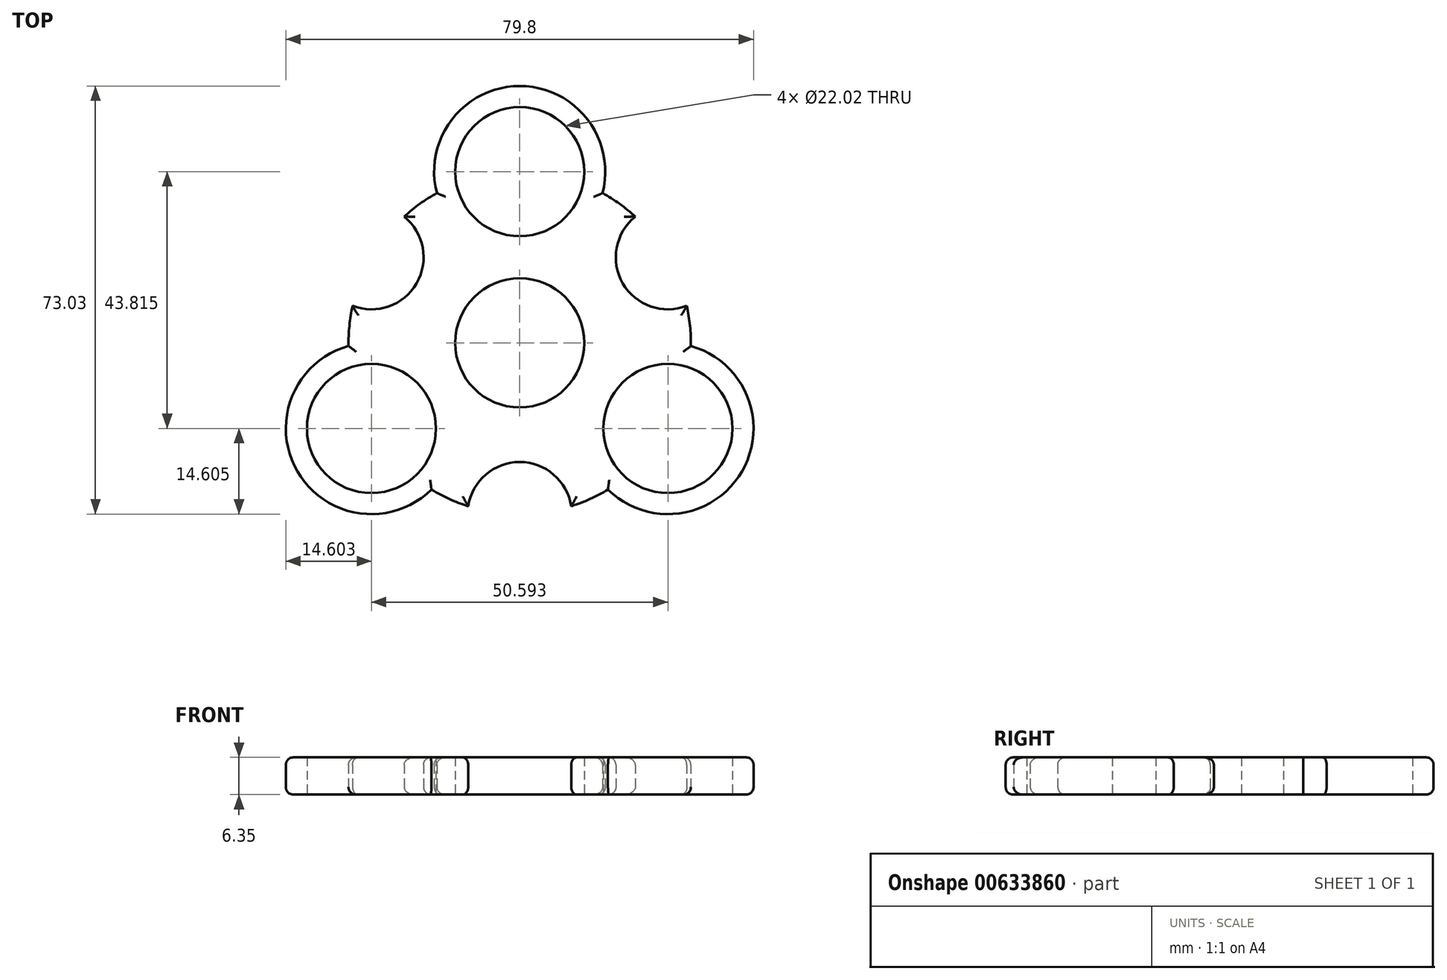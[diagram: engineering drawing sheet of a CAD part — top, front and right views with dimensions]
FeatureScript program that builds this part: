
annotation { "Feature Type Name" : "Feature", "Feature Type Description" : "" }
export const myFeature = defineFeature(function(context is Context, id is Id, definition is map)
    precondition{}
    {
        {
            var Q0;
            Q0=qCreatedBy(makeId("Top.planeOp"),FACE);
            var sketch = newSketch(context, id + "F0", { "sketchPlane" : qUnion([Q0])});
            skCircle(sketch, "E0", {"center": v(0, 0) * mm, "radius": 11.01 * mm});
            skCircle(sketch, "E1", {"center": v(0, 0) * mm, "radius": 14.6 * mm});
            skLineSegment(sketch, "E2", {"start": v(0, 0) * mm, "end": v(0, 29.21) * mm});
            skLineSegment(sketch, "E3", {"start": v(0, 0) * mm, "end": v(-25.3, -14.6) * mm});
            skLineSegment(sketch, "E4", {"start": v(0, 0) * mm, "end": v(25.3, -14.6) * mm});
            skCircle(sketch, "E5", {"center": v(0, 29.21) * mm, "radius": 11.01 * mm});
            skCircle(sketch, "E6", {"center": v(0, 29.21) * mm, "radius": 14.6 * mm});
            skCircle(sketch, "E7", {"center": v(-25.3, -14.6) * mm, "radius": 11.01 * mm});
            skCircle(sketch, "E8", {"center": v(25.3, -14.6) * mm, "radius": 11.01 * mm});
            skCircle(sketch, "E9", {"center": v(25.3, -14.6) * mm, "radius": 14.6 * mm});
            skCircle(sketch, "E10", {"center": v(-25.3, -14.6) * mm, "radius": 14.6 * mm});
            skArc(sketch, "E11", {"start": v(-14.14, 25.56) * mm, "mid": v(-25.3, 14.6) * mm, "end": v(-29.2, -0.53) * mm});
            skArc(sketch, "E12.trimOffspring", {"start": v(29.2, -0.53) * mm, "mid": v(25.3, 14.6) * mm, "end": v(14.14, 25.56) * mm});
            skArc(sketch, "E13.trimOffspring", {"start": v(-15.06, -25.03) * mm, "mid": v(0, -29.2) * mm, "end": v(15.06, -25.03) * mm});
            skArc(sketch, "E14", {"start": v(-28.52, 6.32) * mm, "mid": v(-17.6, 10.16) * mm, "end": v(-19.73, 21.54) * mm});
            skArc(sketch, "E15", {"start": v(19.73, 21.54) * mm, "mid": v(17.6, 10.16) * mm, "end": v(28.52, 6.32) * mm});
            skArc(sketch, "E16", {"start": v(8.79, -27.86) * mm, "mid": v(0, -20.32) * mm, "end": v(-8.79, -27.86) * mm});
            skSolve(sketch);
        }
        {
            var Q0;
            Q0=makeQuery(id+"F0.imprint","IMPRINT",FACE,{"disambiguationData":[TD([[makeQuery(id+"F0.imprint","IMPRINT",EDGE,{"derivedFrom":sQuery(id+"F0.wireOp",EDGE,"E5")}),-1.0]])]});
            var Q1;
            Q1=makeQuery(id+"F0.imprint","IMPRINT",FACE,{"disambiguationData":[TD([[makeQuery(id+"F0.imprint","IMPRINT",EDGE,{"derivedFrom":sQuery(id+"F0.wireOp",EDGE,"E7")}),-1.0]])]});
            var Q2;
            Q2=makeQuery(id+"F0.imprint","IMPRINT",FACE,{"disambiguationData":[TD([[makeQuery(id+"F0.imprint","IMPRINT",EDGE,{"derivedFrom":sQuery(id+"F0.wireOp",EDGE,"E8")}),-1.0]])]});
            var Q3;
            {var subQ3=sQuery(id+"F0.wireOp",EDGE,"E14");Q3=makeQuery(id+"F0.imprint","IMPRINT",FACE,{"disambiguationData":[TD([[makeQuery(id+"F0.imprint","IMPRINT",EDGE,{"derivedFrom":subQ3}),-1.0]])]});}
            var Q4;
            {var subQ3=sQuery(id+"F0.wireOp",EDGE,"E16");Q4=makeQuery(id+"F0.imprint","IMPRINT",FACE,{"disambiguationData":[TD([[makeQuery(id+"F0.imprint","IMPRINT",EDGE,{"derivedFrom":subQ3}),-1.0]])]});}
            var Q5;
            {var subQ3=sQuery(id+"F0.wireOp",EDGE,"E15");Q5=makeQuery(id+"F0.imprint","IMPRINT",FACE,{"disambiguationData":[TD([[makeQuery(id+"F0.imprint","IMPRINT",EDGE,{"derivedFrom":subQ3}),-1.0]])]});}
            var Q6;
            {var subQ0=sQuery(id+"F0.wireOp",EDGE,"E3");var subQ1=sQuery(id+"F0.wireOp",EDGE,"E0");var subQ2=makeQuery(id+"F0.imprint","INTERSECT",VERTEX,{"derivedFrom":[subQ1,subQ0]});Q6=makeQuery(id+"F0.imprint","IMPRINT",FACE,{"disambiguationData":[TD([[makeQuery(id+"F0.imprint","IMPRINT",EDGE,{"disambiguationData":[TD([[subQ2,1.0]])],"derivedFrom":subQ1}),-1.0]])]});}
            var Q7;
            {var subQ0=sQuery(id+"F0.wireOp",EDGE,"E3");var subQ1=sQuery(id+"F0.wireOp",EDGE,"E0");var subQ2=makeQuery(id+"F0.imprint","INTERSECT",VERTEX,{"derivedFrom":[subQ1,subQ0]});Q7=makeQuery(id+"F0.imprint","IMPRINT",FACE,{"disambiguationData":[TD([[makeQuery(id+"F0.imprint","IMPRINT",EDGE,{"disambiguationData":[TD([[subQ2,-1.0]])],"derivedFrom":subQ1}),-1.0]])]});}
            var Q8;
            {var subQ0=sQuery(id+"F0.wireOp",EDGE,"E2");var subQ1=sQuery(id+"F0.wireOp",EDGE,"E0");var subQ2=makeQuery(id+"F0.imprint","INTERSECT",VERTEX,{"derivedFrom":[subQ1,subQ0]});Q8=makeQuery(id+"F0.imprint","IMPRINT",FACE,{"disambiguationData":[TD([[makeQuery(id+"F0.imprint","IMPRINT",EDGE,{"disambiguationData":[TD([[subQ2,1.0]])],"derivedFrom":subQ1}),-1.0]])]});}
            extrude(context, id + "F1", {"entities" : qUnion([Q0, Q1, Q2, Q3, Q4, Q5, Q6, Q7, Q8]), "depth" : 6.35 * mm, "offsetDistance" : 25.4 * mm});
        }
        {
            var Q0;
            Q0=makeQuery(id+"F1.opExtrude","CAP_EDGE",EDGE,{"disambiguationData":[OSD([sQuery(id+"F0.wireOp",EDGE,"E6")])],"isStart":false});
            var Q1;
            Q1=makeQuery(id+"F1.opExtrude","CAP_EDGE",EDGE,{"disambiguationData":[OSD([sQuery(id+"F0.wireOp",EDGE,"E14")])],"isStart":false});
            var Q2;
            Q2=makeQuery(id+"F1.opExtrude","CAP_EDGE",EDGE,{"disambiguationData":[OSD([sQuery(id+"F0.wireOp",EDGE,"E10")])],"isStart":false});
            var Q3;
            {var subQ0=sQuery(id+"F0.wireOp",EDGE,"E11");Q3=makeQuery(id+"F1.opExtrude","CAP_EDGE",EDGE,{"disambiguationData":[OSD([subQ0]),TDD([makeQuery(id+"F0.imprint","IMPRINT",EDGE,{"disambiguationData":[TD([[makeQuery(id+"F0.imprint","INTERSECT",VERTEX,{"derivedFrom":[sQuery(id+"F0.wireOp",EDGE,"E10"),subQ0]}),1.0]])],"derivedFrom":subQ0})])],"isStart":false});}
            var Q4;
            {var subQ0=sQuery(id+"F0.wireOp",EDGE,"E13.trimOffspring");Q4=makeQuery(id+"F1.opExtrude","CAP_EDGE",EDGE,{"disambiguationData":[OSD([subQ0]),TDD([makeQuery(id+"F0.imprint","IMPRINT",EDGE,{"disambiguationData":[TD([[makeQuery(id+"F0.imprint","INTERSECT",VERTEX,{"derivedFrom":[sQuery(id+"F0.wireOp",EDGE,"E10"),subQ0]}),-1.0]])],"derivedFrom":subQ0})])],"isStart":false});}
            var Q5;
            Q5=makeQuery(id+"F1.opExtrude","CAP_EDGE",EDGE,{"disambiguationData":[OSD([sQuery(id+"F0.wireOp",EDGE,"E16")])],"isStart":false});
            var Q6;
            {var subQ0=sQuery(id+"F0.wireOp",EDGE,"E13.trimOffspring");Q6=makeQuery(id+"F1.opExtrude","CAP_EDGE",EDGE,{"disambiguationData":[OSD([subQ0]),TDD([makeQuery(id+"F0.imprint","IMPRINT",EDGE,{"disambiguationData":[TD([[makeQuery(id+"F0.imprint","INTERSECT",VERTEX,{"derivedFrom":[sQuery(id+"F0.wireOp",EDGE,"E9"),subQ0]}),1.0]])],"derivedFrom":subQ0})])],"isStart":false});}
            var Q7;
            Q7=makeQuery(id+"F1.opExtrude","CAP_EDGE",EDGE,{"disambiguationData":[OSD([sQuery(id+"F0.wireOp",EDGE,"E9")])],"isStart":false});
            var Q8;
            {var subQ0=sQuery(id+"F0.wireOp",EDGE,"E12.trimOffspring");Q8=makeQuery(id+"F1.opExtrude","CAP_EDGE",EDGE,{"disambiguationData":[OSD([subQ0]),TDD([makeQuery(id+"F0.imprint","IMPRINT",EDGE,{"disambiguationData":[TD([[makeQuery(id+"F0.imprint","INTERSECT",VERTEX,{"derivedFrom":[sQuery(id+"F0.wireOp",EDGE,"E9"),subQ0]}),-1.0]])],"derivedFrom":subQ0})])],"isStart":false});}
            var Q9;
            Q9=makeQuery(id+"F1.opExtrude","CAP_EDGE",EDGE,{"disambiguationData":[OSD([sQuery(id+"F0.wireOp",EDGE,"E15")])],"isStart":false});
            var Q10;
            {var subQ0=sQuery(id+"F0.wireOp",EDGE,"E12.trimOffspring");Q10=makeQuery(id+"F1.opExtrude","CAP_EDGE",EDGE,{"disambiguationData":[OSD([subQ0]),TDD([makeQuery(id+"F0.imprint","IMPRINT",EDGE,{"disambiguationData":[TD([[makeQuery(id+"F0.imprint","INTERSECT",VERTEX,{"derivedFrom":[sQuery(id+"F0.wireOp",EDGE,"E6"),subQ0]}),1.0]])],"derivedFrom":subQ0})])],"isStart":false});}
            var Q11;
            {var subQ0=sQuery(id+"F0.wireOp",EDGE,"E11");Q11=makeQuery(id+"F1.opExtrude","CAP_EDGE",EDGE,{"disambiguationData":[OSD([subQ0]),TDD([makeQuery(id+"F0.imprint","IMPRINT",EDGE,{"disambiguationData":[TD([[makeQuery(id+"F0.imprint","INTERSECT",VERTEX,{"derivedFrom":[sQuery(id+"F0.wireOp",EDGE,"E6"),subQ0]}),-1.0]])],"derivedFrom":subQ0})])],"isStart":false});}
            var Q12;
            Q12=makeQuery(id+"F1.opExtrude","CAP_EDGE",EDGE,{"disambiguationData":[OSD([sQuery(id+"F0.wireOp",EDGE,"E6")])],"isStart":true});
            var Q13;
            {var subQ0=sQuery(id+"F0.wireOp",EDGE,"E12.trimOffspring");Q13=makeQuery(id+"F1.opExtrude","CAP_EDGE",EDGE,{"disambiguationData":[OSD([subQ0]),TDD([makeQuery(id+"F0.imprint","IMPRINT",EDGE,{"disambiguationData":[TD([[makeQuery(id+"F0.imprint","INTERSECT",VERTEX,{"derivedFrom":[sQuery(id+"F0.wireOp",EDGE,"E6"),subQ0]}),1.0]])],"derivedFrom":subQ0})])],"isStart":true});}
            var Q14;
            Q14=makeQuery(id+"F1.opExtrude","CAP_EDGE",EDGE,{"disambiguationData":[OSD([sQuery(id+"F0.wireOp",EDGE,"E15")])],"isStart":true});
            var Q15;
            {var subQ0=sQuery(id+"F0.wireOp",EDGE,"E12.trimOffspring");Q15=makeQuery(id+"F1.opExtrude","CAP_EDGE",EDGE,{"disambiguationData":[OSD([subQ0]),TDD([makeQuery(id+"F0.imprint","IMPRINT",EDGE,{"disambiguationData":[TD([[makeQuery(id+"F0.imprint","INTERSECT",VERTEX,{"derivedFrom":[sQuery(id+"F0.wireOp",EDGE,"E9"),subQ0]}),-1.0]])],"derivedFrom":subQ0})])],"isStart":true});}
            var Q16;
            Q16=makeQuery(id+"F1.opExtrude","CAP_EDGE",EDGE,{"disambiguationData":[OSD([sQuery(id+"F0.wireOp",EDGE,"E9")])],"isStart":true});
            var Q17;
            {var subQ0=sQuery(id+"F0.wireOp",EDGE,"E13.trimOffspring");Q17=makeQuery(id+"F1.opExtrude","CAP_EDGE",EDGE,{"disambiguationData":[OSD([subQ0]),TDD([makeQuery(id+"F0.imprint","IMPRINT",EDGE,{"disambiguationData":[TD([[makeQuery(id+"F0.imprint","INTERSECT",VERTEX,{"derivedFrom":[sQuery(id+"F0.wireOp",EDGE,"E9"),subQ0]}),1.0]])],"derivedFrom":subQ0})])],"isStart":true});}
            var Q18;
            Q18=makeQuery(id+"F1.opExtrude","CAP_EDGE",EDGE,{"disambiguationData":[OSD([sQuery(id+"F0.wireOp",EDGE,"E16")])],"isStart":true});
            var Q19;
            {var subQ0=sQuery(id+"F0.wireOp",EDGE,"E13.trimOffspring");Q19=makeQuery(id+"F1.opExtrude","CAP_EDGE",EDGE,{"disambiguationData":[OSD([subQ0]),TDD([makeQuery(id+"F0.imprint","IMPRINT",EDGE,{"disambiguationData":[TD([[makeQuery(id+"F0.imprint","INTERSECT",VERTEX,{"derivedFrom":[sQuery(id+"F0.wireOp",EDGE,"E10"),subQ0]}),-1.0]])],"derivedFrom":subQ0})])],"isStart":true});}
            var Q20;
            Q20=makeQuery(id+"F1.opExtrude","CAP_EDGE",EDGE,{"disambiguationData":[OSD([sQuery(id+"F0.wireOp",EDGE,"E10")])],"isStart":true});
            var Q21;
            {var subQ0=sQuery(id+"F0.wireOp",EDGE,"E11");Q21=makeQuery(id+"F1.opExtrude","CAP_EDGE",EDGE,{"disambiguationData":[OSD([subQ0]),TDD([makeQuery(id+"F0.imprint","IMPRINT",EDGE,{"disambiguationData":[TD([[makeQuery(id+"F0.imprint","INTERSECT",VERTEX,{"derivedFrom":[sQuery(id+"F0.wireOp",EDGE,"E10"),subQ0]}),1.0]])],"derivedFrom":subQ0})])],"isStart":true});}
            var Q22;
            {var subQ0=sQuery(id+"F0.wireOp",EDGE,"E11");Q22=makeQuery(id+"F1.opExtrude","CAP_EDGE",EDGE,{"disambiguationData":[OSD([subQ0]),TDD([makeQuery(id+"F0.imprint","IMPRINT",EDGE,{"disambiguationData":[TD([[makeQuery(id+"F0.imprint","INTERSECT",VERTEX,{"derivedFrom":[sQuery(id+"F0.wireOp",EDGE,"E6"),subQ0]}),-1.0]])],"derivedFrom":subQ0})])],"isStart":true});}
            var Q23;
            Q23=makeQuery(id+"F1.opExtrude","CAP_EDGE",EDGE,{"disambiguationData":[OSD([sQuery(id+"F0.wireOp",EDGE,"E14")])],"isStart":true});
            fillet(context, id + "F2", {"entities" : qUnion([Q0, Q1, Q2, Q3, Q4, Q5, Q6, Q7, Q8, Q9, Q10, Q11, Q12, Q13, Q14, Q15, Q16, Q17, Q18, Q19, Q20, Q21, Q22, Q23]), "radius" : 1.27 * mm, "tangentPropagation" : true, "allowEdgeOverflow" : false});
        }
    });
